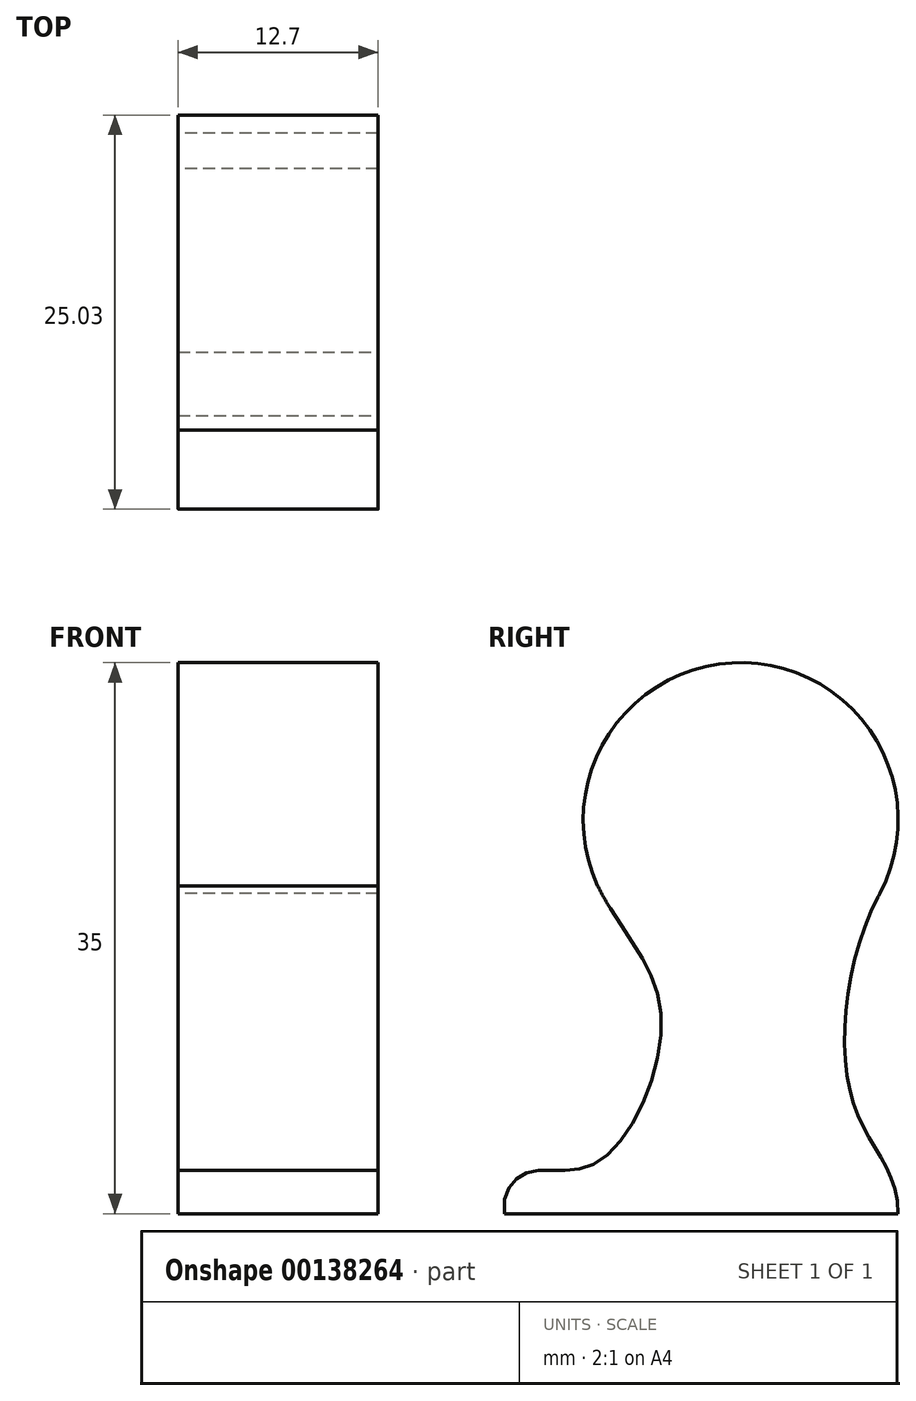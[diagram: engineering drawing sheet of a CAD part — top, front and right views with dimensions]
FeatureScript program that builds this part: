
annotation { "Feature Type Name" : "Feature", "Feature Type Description" : "" }
export const myFeature = defineFeature(function(context is Context, id is Id, definition is map)
    precondition{}
    {
        {
            var Q0;
            Q0=qCreatedBy(makeId("Right.planeOp"),FACE);
            var sketch = newSketch(context, id + "F0", { "sketchPlane" : qUnion([Q0])});
            skLineSegment(sketch, "E0", {"start": v(0, 0) * mm, "end": v(-25, 0) * mm});
            skCircle(sketch, "E1", {"center": v(-10, 25) * mm, "radius": 10 * mm});
            skLineSegment(sketch, "E2", {"start": v(0, 0) * mm, "end": v(0, 25) * mm, "construction": true});
            skFitSpline(sketch, "E3", {"points": [v(0, 0) * mm, v(-2.83, 6.97) * mm, v(-1.15, 20.35) * mm], "startDerivative": vector(0, 20.11) * mm, "endDerivative": vector(11.4, 20.6) * mm});
            skFitSpline(sketch, "E4", {"points": [v(-25, 0) * mm, v(-23.45, 2.63) * mm, v(-19.12, 3.24) * mm, v(-15.07, 12.69) * mm, v(-19.09, 20.83) * mm], "startDerivative": vector(-3.57, 23.73) * mm, "endDerivative": vector(-14.7, 29.53) * mm});
            skSolve(sketch);
        }
        {
            var Q0;
            Q0=makeQuery(id+"F0.imprint","IMPRINT",FACE,{"disambiguationData":[TD([[makeQuery(id+"F0.imprint","IMPRINT",EDGE,{"derivedFrom":sQuery(id+"F0.wireOp",EDGE,"OwjaO6Rb-1F63-9NWU-ANYM-E9JF4rU3TIMN")}),-1.0]])]});
            var Q1;
            {var subQ0=sQuery(id+"F0.wireOp",EDGE,"E0");Q1=makeQuery(id+"F0.imprint","IMPRINT",FACE,{"disambiguationData":[TD([[makeQuery(id+"F0.imprint","IMPRINT",EDGE,{"derivedFrom":subQ0}),-1.0]])]});}
            var Q2;
            {var subQ0=sQuery(id+"F0.wireOp",EDGE,"E4");var subQ1=sQuery(id+"F0.wireOp",EDGE,"E1");var subQ2=makeQuery(id+"F0.imprint","INTERSECT",VERTEX,{"disambiguationData":[OD(1.0)],"derivedFrom":[subQ1,subQ0]});Q2=makeQuery(id+"F0.imprint","IMPRINT",FACE,{"disambiguationData":[TD([[makeQuery(id+"F0.imprint","IMPRINT",EDGE,{"disambiguationData":[TD([[subQ2,-1.0]])],"derivedFrom":subQ1}),1.0]])]});}
            extrude(context, id + "F1", {"entities" : qUnion([Q0, Q1, Q2]), "depth" : 12.7 * mm});
        }
    });
